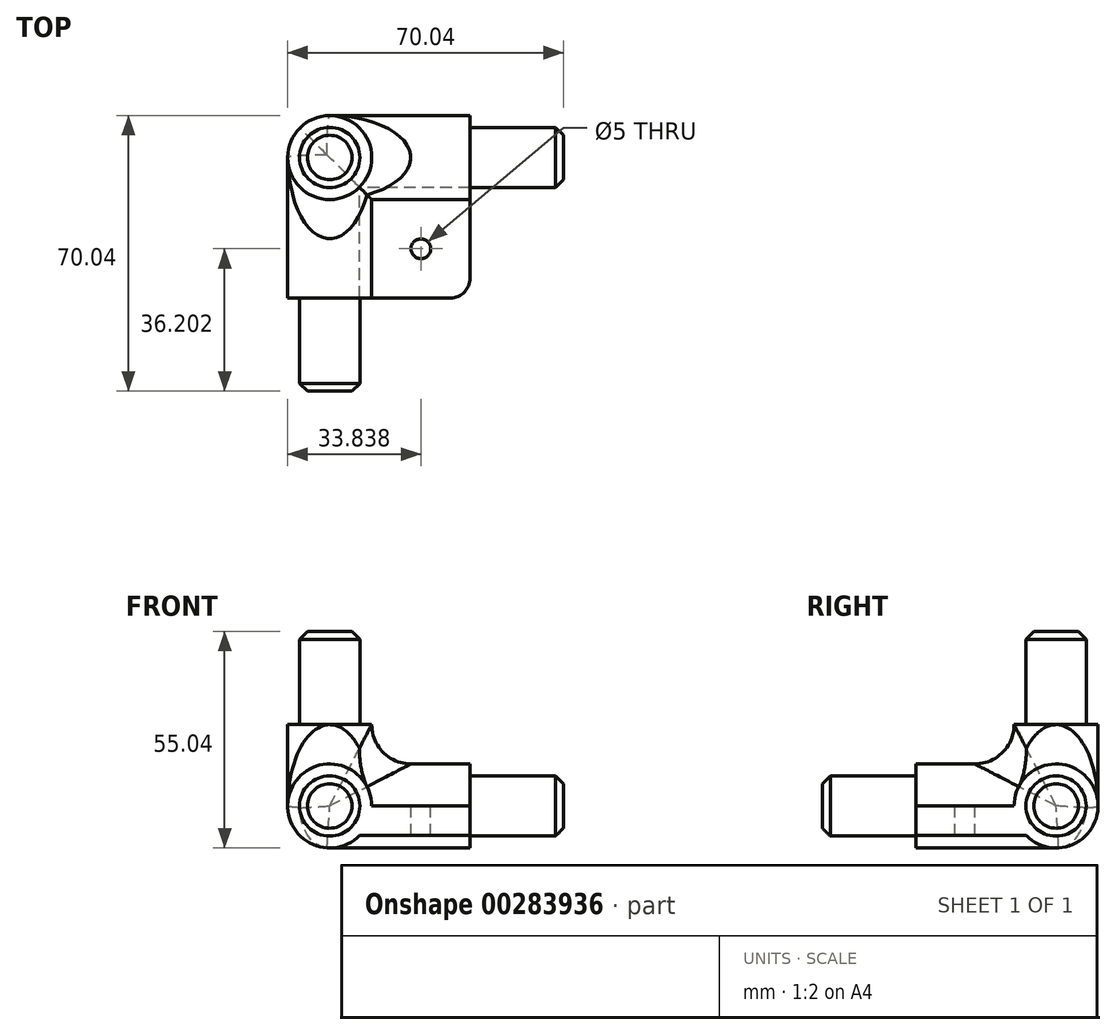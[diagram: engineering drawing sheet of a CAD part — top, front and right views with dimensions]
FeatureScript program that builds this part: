
annotation { "Feature Type Name" : "Feature", "Feature Type Description" : "" }
export const myFeature = defineFeature(function(context is Context, id is Id, definition is map)
    precondition{}
    {
        {
            var Q0;
            Q0=qCreatedBy(makeId("Front.planeOp"),FACE);
            var sketch = newSketch(context, id + "F0", { "sketchPlane" : qUnion([Q0])});
            skCircle(sketch, "E0", {"center": v(0, 0) * mm, "radius": 10.67 * mm});
            skSolve(sketch);
        }
        {
            var Q0;
            Q0=qSketchRegion(id+"F0",true);
            extrude(context, id + "F1", {"entities" : qUnion([Q0]), "depth" : 21.34 * mm / 2 + 25 * mm});
        }
        {
            var Q0;
            Q0=qCreatedBy(makeId("Top.planeOp"),FACE);
            var sketch = newSketch(context, id + "F2", { "sketchPlane" : qUnion([Q0])});
            skCircle(sketch, "E1", {"center": v(0, 0) * mm, "radius": 10.67 * mm});
            skSolve(sketch);
        }
        {
            var Q0;
            Q0=qSketchRegion(id+"F2",true);
            extrude(context, id + "F3", {"entities" : qUnion([Q0]), "operationType" : NewBodyOperationType.ADD, "depth" : 21.34 * mm / 2 + 10 * mm});
        }
        {
            var Q0;
            Q0=qCreatedBy(makeId("Right.planeOp"),FACE);
            var sketch = newSketch(context, id + "F4", { "sketchPlane" : qUnion([Q0])});
            skCircle(sketch, "E2", {"center": v(0, 0) * mm, "radius": 10.67 * mm});
            skSolve(sketch);
        }
        {
            var Q0;
            Q0=qSketchRegion(id+"F4",true);
            extrude(context, id + "F5", {"entities" : qUnion([Q0]), "operationType" : NewBodyOperationType.ADD, "depth" : 21.34 * mm / 2 + 25 * mm});
        }
        {
            var Q0;
            Q0=makeQuery(id+"F1.opExtrude","CAP_FACE",FACE,{"disambiguationData":[OSD([sQuery(id+"F0.wireOp",EDGE,"E0")])],"isStart":true});
            var Q1;
            Q1=makeQuery(id+"F3.opExtrude","SWEPT_FACE",FACE,{"disambiguationData":[OSD([sQuery(id+"F2.wireOp",EDGE,"E1")])]});
            extrude(context, id + "F6", {"entities" : qUnion([Q0]), "operationType" : NewBodyOperationType.ADD, "endBound" : BoundingType.UP_TO_SURFACE, "endBoundEntityFace" : qUnion([Q1]), "depth" : 25 * mm});
        }
        {
            var Q0;
            Q0=makeQuery(id+"F6.opExtrude","SWEPT_FACE",FACE,{"disambiguationData":[OSD([sQuery(id+"F0.wireOp",EDGE,"E0"),sQuery(id+"F4.wireOp",EDGE,"E2")])]});
            extrude(context, id + "F7", {"entities" : qUnion([Q0]), "operationType" : NewBodyOperationType.REMOVE, "endBound" : BoundingType.THROUGH_ALL, "oppositeDirection" : true, "depth" : 25 * mm});
        }
        {
            var Q0;
            Q0=makeQuery(id+"F5.opExtrude","CAP_FACE",FACE,{"disambiguationData":[OSD([sQuery(id+"F4.wireOp",EDGE,"E2")])],"isStart":false});
            var sketch = newSketch(context, id + "F8", { "sketchPlane" : qUnion([Q0])});
            skCircle(sketch, "E3", {"center": v(0, 0) * mm, "radius": 7.65 * mm});
            skSolve(sketch);
        }
        {
            var Q0;
            Q0=qSketchRegion(id+"F8",true);
            extrude(context, id + "F9", {"entities" : qUnion([Q0]), "operationType" : NewBodyOperationType.ADD, "depth" : 1.5 * 15.8 * mm});
        }
        {
            var Q0;
            Q0=makeQuery(id+"F1.opExtrude","CAP_FACE",FACE,{"disambiguationData":[OSD([sQuery(id+"F0.wireOp",EDGE,"E0")])],"isStart":false});
            var sketch = newSketch(context, id + "F10", { "sketchPlane" : qUnion([Q0])});
            skCircle(sketch, "E4", {"center": v(0, 0) * mm, "radius": 7.65 * mm});
            skSolve(sketch);
        }
        {
            var Q0;
            Q0=qSketchRegion(id+"F10",true);
            extrude(context, id + "F11", {"entities" : qUnion([Q0]), "operationType" : NewBodyOperationType.ADD, "depth" : 1.5 * 15.8 * mm});
        }
        {
            var Q0;
            Q0=makeQuery(id+"F3.opExtrude","CAP_FACE",FACE,{"disambiguationData":[OSD([sQuery(id+"F2.wireOp",EDGE,"E1")])],"isStart":false});
            var sketch = newSketch(context, id + "F12", { "sketchPlane" : qUnion([Q0])});
            skCircle(sketch, "E5", {"center": v(0, 0) * mm, "radius": 7.65 * mm});
            skSolve(sketch);
        }
        {
            var Q0;
            Q0=qSketchRegion(id+"F12",true);
            extrude(context, id + "F13", {"entities" : qUnion([Q0]), "operationType" : NewBodyOperationType.ADD, "depth" : 1.5 * 15.8 * mm});
        }
        {
            var Q0;
            Q0=makeQuery(id+"F13.opExtrude","CAP_EDGE",EDGE,{"disambiguationData":[OSD([sQuery(id+"F12.wireOp",EDGE,"E5")])],"isStart":false});
            var Q1;
            Q1=makeQuery(id+"F9.opExtrude","CAP_EDGE",EDGE,{"disambiguationData":[OSD([sQuery(id+"F8.wireOp",EDGE,"E3")])],"isStart":false});
            var Q2;
            Q2=makeQuery(id+"F11.opExtrude","CAP_EDGE",EDGE,{"disambiguationData":[OSD([sQuery(id+"F10.wireOp",EDGE,"E4")])],"isStart":false});
            chamfer(context, id + "F14", {"entities" : qUnion([Q0, Q1, Q2]), "width" : 2 * mm, "tangentPropagation" : true});
        }
        {
            var Q0;
            Q0=qCreatedBy(makeId("Top.planeOp"),FACE);
            var sketch = newSketch(context, id + "F15", { "sketchPlane" : qUnion([Q0])});
            skLineSegment(sketch, "E6.0", {"start": v(10.67, -35.67) * mm, "end": v(-10.67, -35.67) * mm, "construction": true});
            skLineSegment(sketch, "E6.1", {"start": v(35.67, 10.67) * mm, "end": v(35.67, -10.67) * mm, "construction": true});
            skLineSegment(sketch, "E7.bottom", {"start": v(0, 0) * mm, "end": v(35.67, 0) * mm});
            skLineSegment(sketch, "E7.top", {"start": v(0, -35.67) * mm, "end": v(35.67, -35.67) * mm});
            skLineSegment(sketch, "E7.left", {"start": v(0, 0) * mm, "end": v(0, -35.67) * mm});
            skLineSegment(sketch, "E7.right", {"start": v(35.67, 0) * mm, "end": v(35.67, -35.67) * mm});
            skSolve(sketch);
        }
        {
            var Q0;
            Q0 = qSketchRegion(id + "F15", true);
            extrude(context, id + "F16", {"entities" : qUnion([Q0]), "operationType" : NewBodyOperationType.ADD, "oppositeDirection" : true, "depth" : 7.5 * mm});
        }
        {
            var Q0;
            Q0=makeQuery(id+"F16.opExtrude","SWEPT_EDGE",EDGE,{"disambiguationData":[OSD([sQuery(id+"F15.wireOp",EDGE,"E7.top"),sQuery(id+"F15.wireOp",EDGE,"E7.right")])]});
            fillet(context, id + "F17", {"entities" : qUnion([Q0]), "radius" : 5 * mm, "tangentPropagation" : true, "allowEdgeOverflow" : false});
        }
        {
            var Q0;
            Q0=makeQuery(id+"F16.opExtrude","CAP_FACE",FACE,{"disambiguationData":[OSD([sQuery(id+"F15.wireOp",EDGE,"E7.bottom"),sQuery(id+"F15.wireOp",EDGE,"E7.top"),sQuery(id+"F15.wireOp",EDGE,"E7.left"),sQuery(id+"F15.wireOp",EDGE,"E7.right")])],"isStart":true});
            var sketch = newSketch(context, id + "F18", { "sketchPlane" : qUnion([Q0])});
            skLineSegment(sketch, "E8", {"start": v(23.17, -10.67) * mm, "end": v(23.17, -35.67) * mm, "construction": true});
            skCircle(sketch, "E9", {"center": v(23.17, -23.17) * mm, "radius": 2.5 * mm});
            skSolve(sketch);
        }
        {
            var Q0;
            Q0 = qSketchRegion(id + "F18", true);
            extrude(context, id + "F19", {"entities" : qUnion([Q0]), "operationType" : NewBodyOperationType.REMOVE, "endBound" : BoundingType.THROUGH_ALL, "oppositeDirection" : true, "depth" : 25 * mm});
        }
        {
            var Q0;
            {var subQ0=sQuery(id+"F2.wireOp",EDGE,"E1");Q0=makeQuery(id+"F7.boolean.opBoolean","INTERSECT",EDGE,{"derivedFrom":[makeQuery(id+"F6.boolean.opBoolean","MERGE",FACE,{"derivedFrom":[makeQuery(id+"F3.opExtrude","SWEPT_FACE",FACE,{"disambiguationData":[OSD([subQ0])]}),makeQuery(id+"F6.opExtrude","CAP_FACE",FACE,{"disambiguationData":[OSD([subQ0])],"isStart":false})]}),makeQuery(id+"F7.opExtrude","SWEPT_FACE",FACE,{"disambiguationData":[OSD([sQuery(id+"F4.wireOp",EDGE,"E2")])]})]});}
            fillet(context, id + "F20", {"entities" : qUnion([Q0]), "radius" : 10 * mm, "tangentPropagation" : true, "allowEdgeOverflow" : false});
        }
        {
            var Q0;
            {var subQ0=makeQuery(id+"F3.opExtrude","SWEPT_FACE",FACE,{"disambiguationData":[OSD([sQuery(id+"F2.wireOp",EDGE,"E1")])]});var subQ1=sQuery(id+"F0.wireOp",EDGE,"E0");Q0=makeQuery(id+"F6.boolean.opBoolean","MERGE",EDGE,{"derivedFrom":[makeQuery(id+"F3.boolean.opBoolean","INTERSECT",EDGE,{"derivedFrom":[makeQuery(id+"F1.opExtrude","SWEPT_FACE",FACE,{"disambiguationData":[OSD([subQ1])]}),subQ0]}),makeQuery(id+"F6.opExtrude","TWEAK_EDGE",EDGE,{"derivedFrom":[makeQuery(id+"F1.opExtrude","CAP_EDGE",EDGE,{"disambiguationData":[OSD([subQ1])],"isStart":true}),subQ0]})]});}
            fillet(context, id + "F21", {"entities" : qUnion([Q0]), "radius" : 10 * mm, "tangentPropagation" : true, "allowEdgeOverflow" : false});
        }
    });
